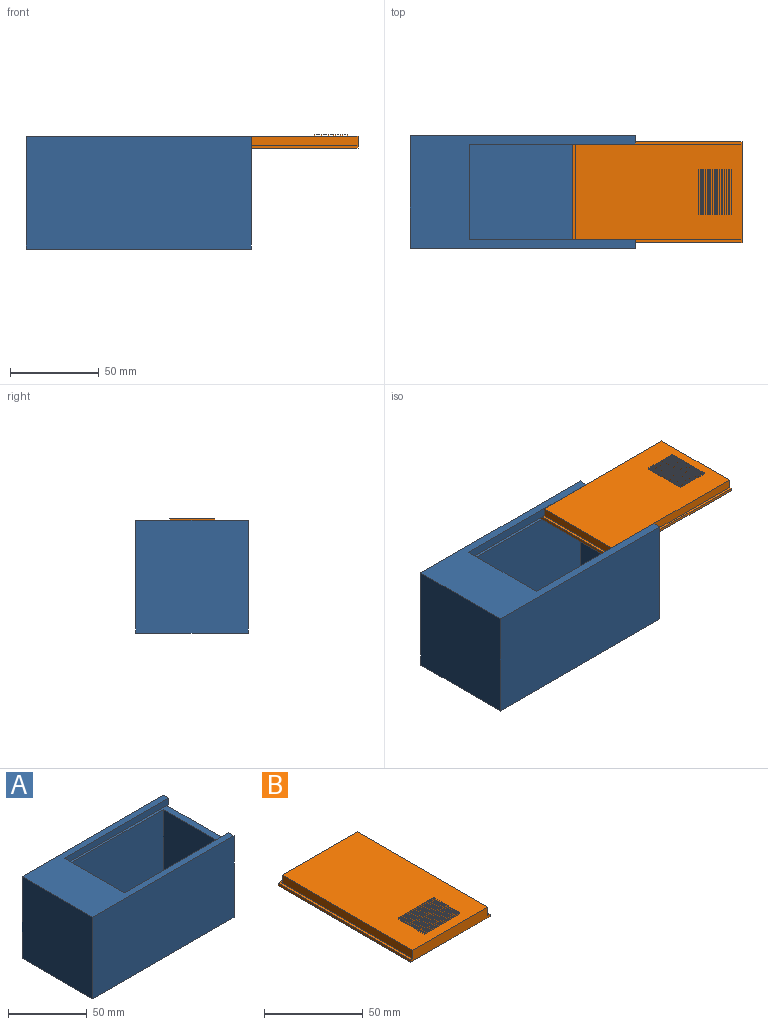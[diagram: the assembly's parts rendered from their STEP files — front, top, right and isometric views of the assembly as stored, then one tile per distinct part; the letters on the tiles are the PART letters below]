
ASSEMBLY  parts=2 mates=3
PART A: 33 faces, bbox 127x63.5x63.5 mm
  f0: plane 53.98x4.93mm, normal (1,0,0), area 266mm2, adj f1,f2,f7,f31
  f1: plane 95.34x6.6mm, normal (0,1,0), area 464mm2, adj f0,f3,f7,f24,f28,f30,f31,f32
  f2: plane 95.34x6.6mm, normal (0,-1,0), area 464mm2, adj f0,f3,f7,f24,f26,f27,f31,f32
  f3: plane 63.5x63.5mm, normal (1,0,0), area 3670.3mm2, adj f1,f2,f5,f7,f9,f10,f24,f25
  f4: plane 36.51x28.58mm, normal (0,-1,0), area 673.2mm2, adj f15,f17,f18,f19,f20,f21,f22,f23
  f5: plane 127x63.5mm, normal (0,1,0), area 7694.3mm2, adj f3,f7,f8,f10,f20,f21,f22,f23
  f6: plane 53.98x52.13mm, normal (1,0,0), area 1167.7mm2, adj f11,f13,f14,f15,f16,f17,f24
  f7: plane 127x63.5mm, normal (0,0,1), area 3009.1mm2, adj f0,f1,f2,f3,f5,f8,f9
  f8: plane 63.5x63.5mm, normal (-1,0,0), area 4032.3mm2, adj f5,f7,f9,f10
  f9: plane 127x63.5mm, normal (0,-1,0), area 8064.5mm2, adj f3,f7,f8,f10
  f10: plane 127x63.5mm, normal (0,0,-1), area 8064.5mm2, adj f3,f5,f8,f9
  f11: plane 88.9x52.13mm, normal (0,1,0), area 4634.7mm2, adj f6,f12,f14,f24
  f12: plane 53.98x52.13mm, normal (-1,0,0), area 2813.9mm2, adj f11,f13,f14,f24
  f13: plane 88.9x52.13mm, normal (0,-1,0), area 4634.7mm2, adj f6,f12,f14,f19,f24
  f14: plane 88.9x53.98mm, normal (0,0,1), area 4798.4mm2, adj f6,f11,f12,f13
  f15: plane 46.36x28.58mm, normal (0,0,-1), area 1324.6mm2, adj f4,f6,f16,f18,f19
  f16: plane 36.51x28.58mm, normal (0,1,0), area 1043.3mm2, adj f6,f15,f17,f18
  f17: plane 46.36x28.58mm, normal (0,0,1), area 1324.6mm2, adj f4,f6,f16,f18,f19
  f18: plane 46.36x36.51mm, normal (1,0,0), area 1692.5mm2, adj f4,f15,f16,f17
  f19: plane 36.51x1.27mm, normal (-1,0,0), area 46.4mm2, adj f4,f13,f15,f17
  f20: plane 12.95x3.49mm, normal (0,0,-1), area 45.2mm2, adj f4,f5,f21,f23
  f21: plane 28.58x3.49mm, normal (-1,0,0), area 99.8mm2, adj f4,f5,f20,f22
  f22: plane 12.95x3.49mm, normal (0,0,1), area 45.2mm2, adj f4,f5,f21,f23
  f23: plane 28.58x3.49mm, normal (1,0,0), area 99.8mm2, adj f4,f5,f20,f22
  f24: plane 95.34x57.33mm, normal (0,0,1), area 667.1mm2, adj f1,f2,f3,f6,f11,f12,f13,f25
  f25: plane 95.33x1.65mm, normal (0,-1,0), area 157.4mm2, adj f3,f24,f26,f27
  f26: plane 95.33x1.68mm, normal (0,0,-1), area 159.8mm2, adj f2,f3,f25,f27
  f27: plane 1.68x1.65mm, normal (1,0,0), area 2.8mm2, adj f2,f24,f25,f26
  f28: plane 95.33x1.68mm, normal (0,0,-1), area 159.8mm2, adj f1,f3,f29,f30
  f29: plane 95.33x1.65mm, normal (0,1,0), area 157.4mm2, adj f3,f24,f28,f30
  f30: plane 1.68x1.65mm, normal (1,0,0), area 2.8mm2, adj f1,f24,f28,f29
  f31: plane 53.98x1.68mm, normal (0,0,-1), area 90.5mm2, adj f0,f1,f2,f32
  f32: plane 53.98x1.68mm, normal (1,0,0), area 90.5mm2, adj f1,f2,f24,f31
PART B: 87 faces, bbox 56.9x95.3x7.4 mm
  f0: plane 93.73x53.85mm, normal (0,0,1), area 4930.8mm2, adj f6,f7,f9,f10,f12,f13,f14,f15
  f1: plane 56.9x1.78mm, normal (0,1,0), area 100.4mm2, adj f2,f3,f4,f5,f6,f7,f8,f11
  f2: plane 95.25x1.52mm, normal (-1,0,0), area 145.2mm2, adj f1,f3,f8,f9
  f3: plane 95.25x56.9mm, normal (0,0,-1), area 5419.3mm2, adj f1,f2,f4,f9
  f4: plane 95.25x1.52mm, normal (1,0,0), area 145.2mm2, adj f1,f3,f5,f9
  f5: plane 95.25x1.52mm, normal (0,0,1), area 145.2mm2, adj f1,f4,f6,f9
  f6: plane 95.25x5.08mm, normal (1,0,0), area 476.5mm2, adj f0,f1,f5,f9,f10,f11
  f7: plane 95.25x5.08mm, normal (-1,0,0), area 476.5mm2, adj f0,f1,f8,f9,f10,f11
  f8: plane 95.25x1.52mm, normal (0,0,1), area 145.2mm2, adj f1,f2,f7,f9
  f9: plane 56.9x6.6mm, normal (0,-1,0), area 360.3mm2, adj f0,f2,f3,f4,f5,f6,f7,f8
  f10: plane 53.85x4.83mm, normal (0,1,0), area 259.9mm2, adj f0,f6,f7,f11
  f11: plane 53.85x1.52mm, normal (0,0,1), area 82.1mm2, adj f1,f6,f7,f10
  f12: plane 25.4x0.76mm, normal (0,-1,0), area 19.4mm2, adj f0,f13,f15,f16
  f13: plane 0.76x0.3mm, normal (1,0,0), area 0.2mm2, adj f0,f12,f14,f16
  f14: plane 25.4x0.76mm, normal (0,1,0), area 19.4mm2, adj f0,f13,f15,f16
  f15: plane 0.76x0.3mm, normal (-1,0,0), area 0.2mm2, adj f0,f12,f14,f16
  f16: plane 25.4x0.3mm, normal (0,0,1), area 7.7mm2, adj f12,f13,f14,f15
  f17: plane 25.4x0.76mm, normal (0,-1,0), area 19.4mm2, adj f0,f18,f20,f21
  f18: plane 0.76x0.3mm, normal (1,0,0), area 0.2mm2, adj f0,f17,f19,f21
  f19: plane 25.4x0.76mm, normal (0,1,0), area 19.4mm2, adj f0,f18,f20,f21
  f20: plane 0.76x0.3mm, normal (-1,0,0), area 0.2mm2, adj f0,f17,f19,f21
  f21: plane 25.4x0.3mm, normal (0,0,1), area 7.7mm2, adj f17,f18,f19,f20
  f22: plane 25.4x0.76mm, normal (0,-1,0), area 19.4mm2, adj f0,f23,f25,f26
  f23: plane 0.76x0.3mm, normal (1,0,0), area 0.2mm2, adj f0,f22,f24,f26
  f24: plane 25.4x0.76mm, normal (0,1,0), area 19.4mm2, adj f0,f23,f25,f26
  f25: plane 0.76x0.3mm, normal (-1,0,0), area 0.2mm2, adj f0,f22,f24,f26
  f26: plane 25.4x0.3mm, normal (0,0,1), area 7.7mm2, adj f22,f23,f24,f25
  f27: plane 25.4x0.76mm, normal (0,-1,0), area 19.4mm2, adj f0,f28,f30,f31
  f28: plane 0.76x0.31mm, normal (1,0,0), area 0.2mm2, adj f0,f27,f29,f31
  f29: plane 25.4x0.76mm, normal (0,1,0), area 19.4mm2, adj f0,f28,f30,f31
  f30: plane 0.76x0.31mm, normal (-1,0,0), area 0.2mm2, adj f0,f27,f29,f31
  f31: plane 25.4x0.31mm, normal (0,0,1), area 7.7mm2, adj f27,f28,f29,f30
  f32: plane 25.4x0.76mm, normal (0,-1,0), area 19.4mm2, adj f0,f33,f35,f36
  f33: plane 0.76x0.31mm, normal (1,0,0), area 0.2mm2, adj f0,f32,f34,f36
  f34: plane 25.4x0.76mm, normal (0,1,0), area 19.4mm2, adj f0,f33,f35,f36
  f35: plane 0.76x0.31mm, normal (-1,0,0), area 0.2mm2, adj f0,f32,f34,f36
  f36: plane 25.4x0.31mm, normal (0,0,1), area 7.7mm2, adj f32,f33,f34,f35
  f37: plane 25.4x0.76mm, normal (0,-1,0), area 19.4mm2, adj f0,f38,f40,f41
  f38: plane 0.76x0.3mm, normal (1,0,0), area 0.2mm2, adj f0,f37,f39,f41
  f39: plane 25.4x0.76mm, normal (0,1,0), area 19.4mm2, adj f0,f38,f40,f41
  f40: plane 0.76x0.3mm, normal (-1,0,0), area 0.2mm2, adj f0,f37,f39,f41
  f41: plane 25.4x0.3mm, normal (0,0,1), area 7.7mm2, adj f37,f38,f39,f40
  f42: plane 25.4x0.76mm, normal (0,-1,0), area 19.4mm2, adj f0,f43,f45,f46
  f43: plane 0.76x0.3mm, normal (1,0,0), area 0.2mm2, adj f0,f42,f44,f46
  f44: plane 25.4x0.76mm, normal (0,1,0), area 19.4mm2, adj f0,f43,f45,f46
  f45: plane 0.76x0.3mm, normal (-1,0,0), area 0.2mm2, adj f0,f42,f44,f46
  f46: plane 25.4x0.3mm, normal (0,0,1), area 7.7mm2, adj f42,f43,f44,f45
  f47: plane 25.4x0.76mm, normal (0,-1,0), area 19.4mm2, adj f0,f48,f50,f51
  f48: plane 0.76x0.31mm, normal (1,0,0), area 0.2mm2, adj f0,f47,f49,f51
  f49: plane 25.4x0.76mm, normal (0,1,0), area 19.4mm2, adj f0,f48,f50,f51
  f50: plane 0.76x0.31mm, normal (-1,0,0), area 0.2mm2, adj f0,f47,f49,f51
  f51: plane 25.4x0.31mm, normal (0,0,1), area 7.7mm2, adj f47,f48,f49,f50
  f52: plane 25.4x0.76mm, normal (0,-1,0), area 19.4mm2, adj f0,f53,f55,f56
  f53: plane 0.76x0.31mm, normal (1,0,0), area 0.2mm2, adj f0,f52,f54,f56
  f54: plane 25.4x0.76mm, normal (0,1,0), area 19.4mm2, adj f0,f53,f55,f56
  f55: plane 0.76x0.31mm, normal (-1,0,0), area 0.2mm2, adj f0,f52,f54,f56
  f56: plane 25.4x0.31mm, normal (0,0,1), area 7.7mm2, adj f52,f53,f54,f55
  f57: plane 25.4x0.76mm, normal (0,-1,0), area 19.4mm2, adj f0,f58,f60,f61
  f58: plane 0.76x0.3mm, normal (1,0,0), area 0.2mm2, adj f0,f57,f59,f61
  f59: plane 25.4x0.76mm, normal (0,1,0), area 19.4mm2, adj f0,f58,f60,f61
  f60: plane 0.76x0.3mm, normal (-1,0,0), area 0.2mm2, adj f0,f57,f59,f61
  f61: plane 25.4x0.3mm, normal (0,0,1), area 7.7mm2, adj f57,f58,f59,f60
  f62: plane 25.4x0.76mm, normal (0,-1,0), area 19.4mm2, adj f0,f63,f65,f66
  f63: plane 0.76x0.3mm, normal (1,0,0), area 0.2mm2, adj f0,f62,f64,f66
  f64: plane 25.4x0.76mm, normal (0,1,0), area 19.4mm2, adj f0,f63,f65,f66
  f65: plane 0.76x0.3mm, normal (-1,0,0), area 0.2mm2, adj f0,f62,f64,f66
  f66: plane 25.4x0.3mm, normal (0,0,1), area 7.7mm2, adj f62,f63,f64,f65
  f67: plane 25.4x0.76mm, normal (0,-1,0), area 19.4mm2, adj f0,f68,f70,f71
  f68: plane 0.76x0.3mm, normal (1,0,0), area 0.2mm2, adj f0,f67,f69,f71
  f69: plane 25.4x0.76mm, normal (0,1,0), area 19.4mm2, adj f0,f68,f70,f71
  f70: plane 0.76x0.3mm, normal (-1,0,0), area 0.2mm2, adj f0,f67,f69,f71
  f71: plane 25.4x0.3mm, normal (0,0,1), area 7.7mm2, adj f67,f68,f69,f70
  f72: plane 25.4x0.76mm, normal (0,-1,0), area 19.4mm2, adj f0,f73,f75,f76
  f73: plane 0.76x0.31mm, normal (1,0,0), area 0.2mm2, adj f0,f72,f74,f76
  f74: plane 25.4x0.76mm, normal (0,1,0), area 19.4mm2, adj f0,f73,f75,f76
  f75: plane 0.76x0.31mm, normal (-1,0,0), area 0.2mm2, adj f0,f72,f74,f76
  f76: plane 25.4x0.31mm, normal (0,0,1), area 7.7mm2, adj f72,f73,f74,f75
  f77: plane 25.4x0.76mm, normal (0,-1,0), area 19.4mm2, adj f0,f78,f80,f81
  f78: plane 0.76x0.31mm, normal (1,0,0), area 0.2mm2, adj f0,f77,f79,f81
  f79: plane 25.4x0.76mm, normal (0,1,0), area 19.4mm2, adj f0,f78,f80,f81
  f80: plane 0.76x0.31mm, normal (-1,0,0), area 0.2mm2, adj f0,f77,f79,f81
  f81: plane 25.4x0.31mm, normal (0,0,1), area 7.7mm2, adj f77,f78,f79,f80
  f82: plane 25.4x0.76mm, normal (0,-1,0), area 19.4mm2, adj f0,f83,f85,f86
  f83: plane 0.76x0.3mm, normal (1,0,0), area 0.2mm2, adj f0,f82,f84,f86
  f84: plane 25.4x0.76mm, normal (0,1,0), area 19.4mm2, adj f0,f83,f85,f86
  f85: plane 0.76x0.3mm, normal (-1,0,0), area 0.2mm2, adj f0,f82,f84,f86
  f86: plane 25.4x0.3mm, normal (0,0,1), area 7.7mm2, adj f82,f83,f84,f85
PLACE A t=(-16.71,18.58,-27.01)mm
PLACE B rot(axis=(0,0,1),90deg) t=(75.11,21.82,29.89)mm
MATE planar B.f7 <-> A.f1  axis (0,-1,0) through (123.46,23.35,33.95)mm
MATE planar B.f0 <-> A.f7  axis (0,0,1) through (123.5,77.19,36.49)mm
MATE parallel B.f9 <-> A.f3  axis (1,0,0) through (170.36,50.27,29.89)mm
